# Revit family: RWL1
name_source: partatom
category: Lighting Fixtures
units: mm (PartAtom-declared; Revit-internal decimal feet)

## family parameters
Cut with Voids When Loaded = No
Host = Face
Light Source = Yes
OmniClass Number = 23.80.70.11
OmniClass Title = Luminaries for Internal Lighting
Part Type = Normal
Room Calculation Point = No
Round Connector Dimension = Use Diameter
Shared = No

## types (1)
- RWL1
    Apparent Load = 10 VA
    Assembly Code = D5020200
    Color Filter = 16777215
    Default Elevation = 48 "
    Description = RWL1 Ratio
    Dimming Lamp Color Temperature Shift = <None>
    Features = Compact size for mounting heights up to 15ft and spacing up to 75ft
Featuring Micro Strike Optics which maximizes target zone illumination with minimal losses at the house-side,reducing light trespass issues.
Visual comfort standard
Micro Strike optics in Type 3 and 4W distributions
Matching rectilinear form to the Ratio Family
Versatile mounting for multiple lighting applications
Large variety of wattages to target specific lumen outputs
Control options including photo control, occupancy sensing,NX Distributed Intelligence™ and 7-Pin with networked controls
Wall mount, Building Mount luminaire.
    Housing = Paint - Textured Camera Black
    Lamp = LED Lamp
    Load Classification = Lighting
    Manufacturer = EXO
    Material Finish = Paint  -  White
    Model = RWL1
    Opal lens = White Glass
    Photometric Note = For more Photometrics Please vist above Link
    Photometric Web File = RWL1-48L-10-3K7-3.ies
    Power Factor = 1
    Tilt Angle = 60.00°
    URL = https://www.currentlighting.com
    Voltage = 120 V
    Warranty = Five year warranty
    Wattage Comments = 10 W to 47 W
    Watts = 10 W
    zz Length 1 = 23.7 "
    zz Length 2 = 23.7 "

## geometry (parser evidence)
native form markers: Sweep x1
no freeform markers — native parametric forms only
